# Revit family: Скамейка стальная «Монс» Арт 13872
name_source: partatom
category: Антураж
revit_build: Autodesk Revit 2018 (Build: 20180423_1000(x64)
units: mm (PartAtom-declared; Revit-internal decimal feet)

## family parameters
Всегда вертикально = Да
Источник визуального образа = Геометрия семейства
На основе рабочей плоскости = Нет
Общий = Нет
При загрузке вырезать с полостями = Нет
Точка расчета площади = Нет

## types (5) — shared parameters
URL = https://hobbyka.ru
Артикул товара = Арт. 13872
Группа модели = Скамейки
Изготовитель = ООО «Хоббика»
Материал изделия = Сталь, дерево
Цвет лавки = Дерево
Цвет опоры = Сталь

## per-type parameters (varying)
| type | Версия 0,6 м (кресло) | Версия 1,5 м (без спинки) | Версия 1,5 м (со спинкой) | Версия 1,8 м (без спинки) | Версия 1,8 м (со спинкой) | Высота | Длина | Изображение типоразмера | Описание | Ширина |
| Версия 0,6 м (кресло со спинкой) | Да | Нет | Нет | Нет | Нет | 790 мм | 600 мм | Скамейка стальная «Монс» Арт 13872 со спинки.jpg | Скамейка стальная «Монс». Версия 0,6 м (кресло со спинкой) | 670 мм |
| Версия 1,5 м (со спинкой) | Нет | Нет | Да | Нет | Нет | 790 мм | 1500 мм | Скамейка стальная «Монс» Арт 13872 со спинки.jpg | Скамейка стальная «Монс». Версия 1,5 м (со спинкой) | 670 мм |
| Версия 1,8 м (со спинкой) | Нет | Нет | Нет | Нет | Да | 790 мм | 1800 мм | Скамейка стальная «Монс» Арт 13872 со спинки.jpg | Скамейка стальная «Монс». Версия 1,8 м (со спинкой) | 670 мм |
| Версия 1,5 м (без спинки) | Нет | Да | Нет | Нет | Нет | 450 мм | 1500 мм | Скамейка стальная «Монс» Арт 13872 без спинки.jpg | Скамейка стальная «Монс». Версия 1,5 м (без спинки) | 470 мм |
| Версия 1,8 м (без спинки) | Нет | Нет | Нет | Да | Нет | 450 мм | 1800 мм | Скамейка стальная «Монс» Арт 13872 без спинки.jpg | Скамейка стальная «Монс». Версия 1,8 м (без спинки) | 470 мм |
